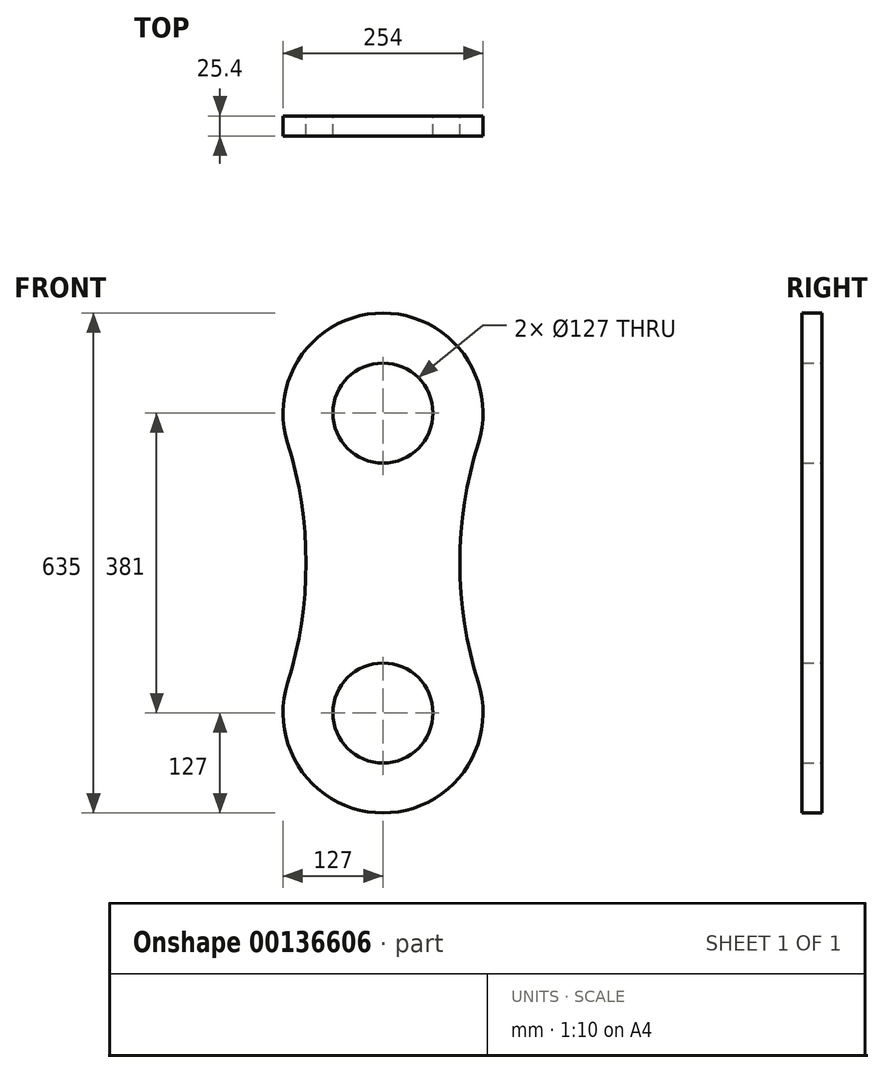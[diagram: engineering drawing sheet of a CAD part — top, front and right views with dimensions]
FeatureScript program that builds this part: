
annotation { "Feature Type Name" : "Feature", "Feature Type Description" : "" }
export const myFeature = defineFeature(function(context is Context, id is Id, definition is map)
    precondition{}
    {
        {
            var Q0;
            Q0=qCreatedBy(makeId("Front.planeOp"),FACE);
            var sketch = newSketch(context, id + "F0", { "sketchPlane" : qUnion([Q0])});
            skArc(sketch, "E0", {"start": v(121.15, 152.4) * mm, "mid": v(0, 317.5) * mm, "end": v(-121.15, 152.4) * mm});
            skArc(sketch, "E1", {"start": v(-121.15, -152.4) * mm, "mid": v(0, -317.5) * mm, "end": v(121.15, -152.4) * mm});
            skCircle(sketch, "E2", {"center": v(0, -190.5) * mm, "radius": 63.5 * mm});
            skCircle(sketch, "E3", {"center": v(0, 190.5) * mm, "radius": 63.5 * mm});
            skArc(sketch, "E4", {"start": v(-121.15, -152.4) * mm, "mid": v(-97.75, 0) * mm, "end": v(-121.15, 152.4) * mm});
            skArc(sketch, "E5", {"start": v(121.15, 152.4) * mm, "mid": v(97.75, 0) * mm, "end": v(121.15, -152.4) * mm});
            skSolve(sketch);
        }
        {
            var Q0;
            Q0=makeQuery(id+"F0.imprint","IMPRINT",FACE,{"disambiguationData":[TD([[makeQuery(id+"F0.imprint","IMPRINT",EDGE,{"derivedFrom":sQuery(id+"F0.wireOp",EDGE,"E0")}),1.0]])]});
            extrude(context, id + "F1", {"entities" : qUnion([Q0]), "depth" : 25.4 * mm});
        }
    });
